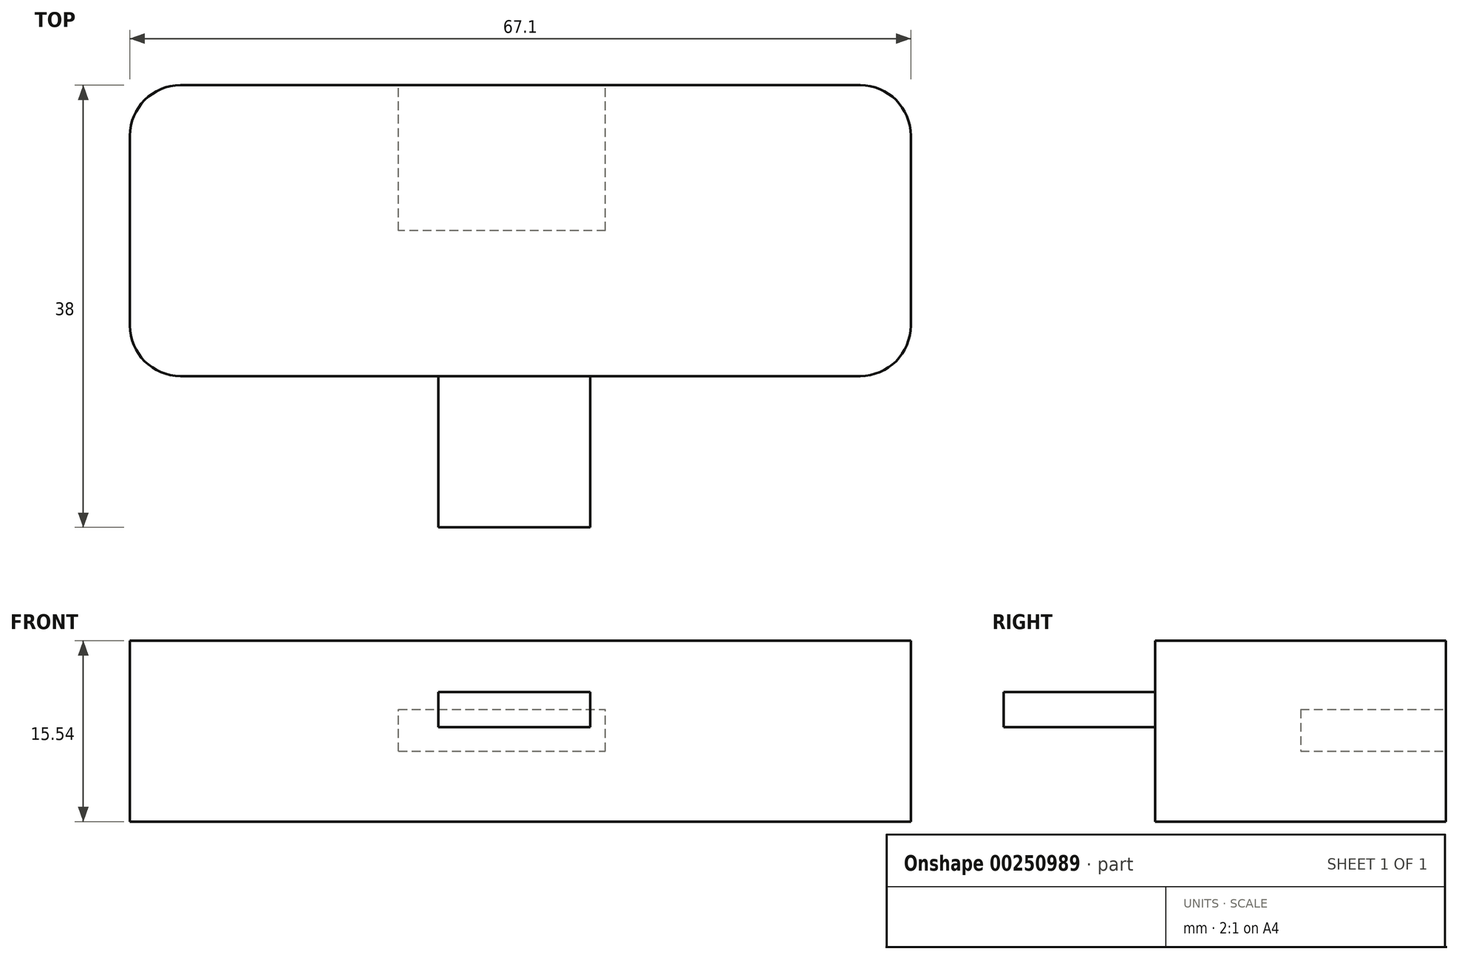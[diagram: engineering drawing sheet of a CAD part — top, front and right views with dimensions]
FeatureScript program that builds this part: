
annotation { "Feature Type Name" : "Feature", "Feature Type Description" : "" }
export const myFeature = defineFeature(function(context is Context, id is Id, definition is map)
    precondition{}
    {
        {
            var Q0;
            Q0=qCreatedBy(makeId("Front.planeOp"),FACE);
            var sketch = newSketch(context, id + "F0", { "sketchPlane" : qUnion([Q0])});
            skLineSegment(sketch, "E0.bottom", {"start": v(-29.68, 5.9) * mm, "end": v(37.42, 5.9) * mm});
            skLineSegment(sketch, "E0.top", {"start": v(-29.68, -9.63) * mm, "end": v(37.42, -9.63) * mm});
            skLineSegment(sketch, "E0.left", {"start": v(-29.68, 5.9) * mm, "end": v(-29.68, -9.63) * mm});
            skLineSegment(sketch, "E0.right", {"start": v(37.42, 5.9) * mm, "end": v(37.42, -9.63) * mm});
            skSolve(sketch);
        }
        {
            var Q0;
            Q0=makeQuery(id+"F0.imprint","IMPRINT",FACE,{"disambiguationData":[TD([[makeQuery(id+"F0.imprint","IMPRINT",EDGE,{"derivedFrom":sQuery(id+"F0.wireOp",EDGE,"E0.bottom")}),-1.0]])]});
            extrude(context, id + "F1", {"entities" : qUnion([Q0]), "depth" : 25 * mm});
        }
        {
            var Q0;
            Q0=makeQuery(id+"F1.opExtrude","CAP_EDGE",EDGE,{"disambiguationData":[OSD([sQuery(id+"F0.wireOp",EDGE,"E0.right")])],"isStart":true});
            var Q1;
            Q1=makeQuery(id+"F1.opExtrude","CAP_EDGE",EDGE,{"disambiguationData":[OSD([sQuery(id+"F0.wireOp",EDGE,"E0.left")])],"isStart":true});
            var Q2;
            Q2=makeQuery(id+"F1.opExtrude","CAP_EDGE",EDGE,{"disambiguationData":[OSD([sQuery(id+"F0.wireOp",EDGE,"E0.right")])],"isStart":false});
            var Q3;
            Q3=makeQuery(id+"F1.opExtrude","CAP_EDGE",EDGE,{"disambiguationData":[OSD([sQuery(id+"F0.wireOp",EDGE,"E0.left")])],"isStart":false});
            fillet(context, id + "F2", {"entities" : qUnion([Q0, Q1, Q2, Q3]), "radius" : 4.35 * mm, "tangentPropagation" : true, "allowEdgeOverflow" : false});
        }
        {
            var Q0;
            Q0=makeQuery(id+"F1.opExtrude","CAP_FACE",FACE,{"disambiguationData":[OSD([sQuery(id+"F0.wireOp",EDGE,"E0.bottom"),sQuery(id+"F0.wireOp",EDGE,"E0.top"),sQuery(id+"F0.wireOp",EDGE,"E0.left"),sQuery(id+"F0.wireOp",EDGE,"E0.right")])],"isStart":false});
            var sketch = newSketch(context, id + "F3", { "sketchPlane" : qUnion([Q0])});
            skLineSegment(sketch, "E1.bottom", {"start": v(-3.18, 1.5) * mm, "end": v(9.88, 1.5) * mm});
            skLineSegment(sketch, "E1.top", {"start": v(-3.18, -1.5) * mm, "end": v(9.88, -1.5) * mm});
            skLineSegment(sketch, "E1.left", {"start": v(-3.18, 1.5) * mm, "end": v(-3.18, -1.5) * mm});
            skLineSegment(sketch, "E1.right", {"start": v(9.88, 1.5) * mm, "end": v(9.88, -1.5) * mm});
            skPoint(sketch, "E1.middle", {"position": v(3.35, 0) * mm});
            skSolve(sketch);
        }
        {
            var Q0;
            Q0=makeQuery(id+"F3.imprint","IMPRINT",FACE,{"disambiguationData":[TD([[makeQuery(id+"F3.imprint","IMPRINT",EDGE,{"derivedFrom":sQuery(id+"F3.wireOp",EDGE,"E1.bottom")}),-1.0]])]});
            extrude(context, id + "F4", {"entities" : qUnion([Q0]), "operationType" : NewBodyOperationType.ADD, "depth" : 13 * mm});
        }
        {
            var Q0;
            Q0=makeQuery(id+"F1.opExtrude","CAP_FACE",FACE,{"disambiguationData":[OSD([sQuery(id+"F0.wireOp",EDGE,"E0.bottom"),sQuery(id+"F0.wireOp",EDGE,"E0.top"),sQuery(id+"F0.wireOp",EDGE,"E0.left"),sQuery(id+"F0.wireOp",EDGE,"E0.right")])],"isStart":true});
            var sketch = newSketch(context, id + "F5", { "sketchPlane" : qUnion([Q0])});
            skLineSegment(sketch, "E2.bottom", {"start": v(-11.19, 0) * mm, "end": v(6.6, 0) * mm});
            skLineSegment(sketch, "E2.top", {"start": v(-11.19, -3.59) * mm, "end": v(6.6, -3.59) * mm});
            skLineSegment(sketch, "E2.left", {"start": v(-11.19, 0) * mm, "end": v(-11.19, -3.59) * mm});
            skLineSegment(sketch, "E2.right", {"start": v(6.6, 0) * mm, "end": v(6.6, -3.59) * mm});
            skSolve(sketch);
        }
        {
            var Q0;
            Q0=makeQuery(id+"F5.imprint","IMPRINT",FACE,{"disambiguationData":[TD([[makeQuery(id+"F5.imprint","IMPRINT",EDGE,{"derivedFrom":sQuery(id+"F5.wireOp",EDGE,"E2.bottom")}),-1.0]])]});
            extrude(context, id + "F6", {"entities" : qUnion([Q0]), "operationType" : NewBodyOperationType.REMOVE, "endBound" : BoundingType.SYMMETRIC, "oppositeDirection" : true, "depth" : 25 * mm});
        }
    });
